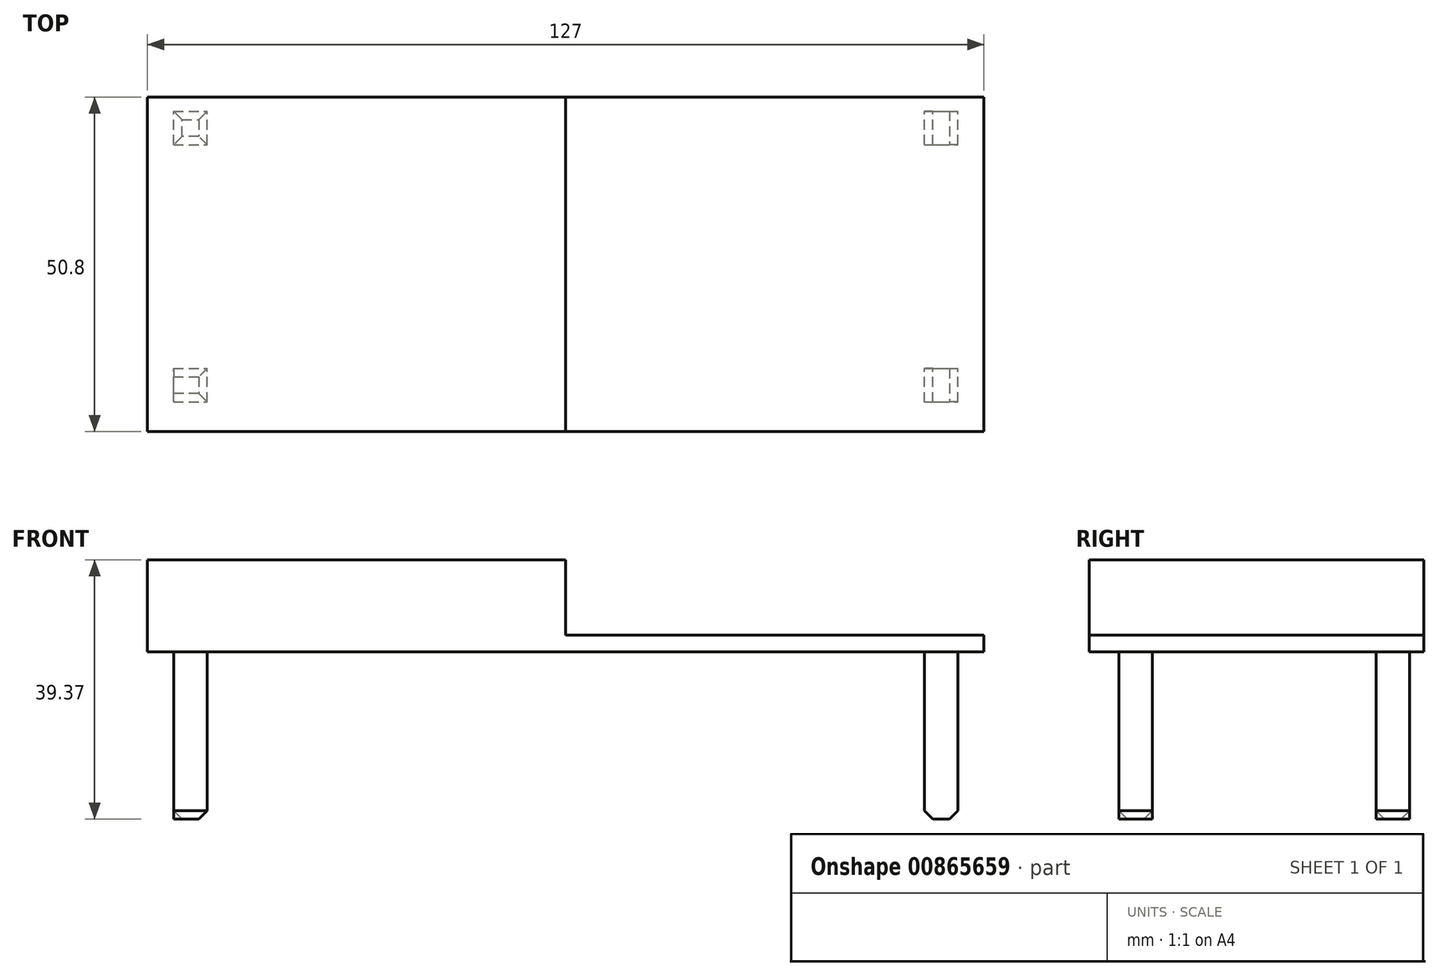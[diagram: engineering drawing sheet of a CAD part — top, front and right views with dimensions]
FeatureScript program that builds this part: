
annotation { "Feature Type Name" : "Feature", "Feature Type Description" : "" }
export const myFeature = defineFeature(function(context is Context, id is Id, definition is map)
    precondition{}
    {
        {
            var Q0;
            Q0=qCreatedBy(makeId("Top.planeOp"),FACE);
            var sketch = newSketch(context, id + "F0", { "sketchPlane" : qUnion([Q0])});
            skLineSegment(sketch, "E0.bottom", {"start": v(-63.73, 34.93) * mm, "end": v(63.27, 34.93) * mm});
            skLineSegment(sketch, "E0.top", {"start": v(-63.73, -15.87) * mm, "end": v(63.27, -15.87) * mm});
            skLineSegment(sketch, "E0.left", {"start": v(-63.73, 34.93) * mm, "end": v(-63.73, -15.87) * mm});
            skLineSegment(sketch, "E0.right", {"start": v(63.27, 34.93) * mm, "end": v(63.27, -15.87) * mm});
            skSolve(sketch);
        }
        {
            var Q0;
            Q0=makeQuery(id+"F0.imprint","IMPRINT",FACE,{"disambiguationData":[TD([[makeQuery(id+"F0.imprint","IMPRINT",EDGE,{"derivedFrom":sQuery(id+"F0.wireOp",EDGE,"E0.bottom")}),-1.0]])]});
            extrude(context, id + "F1", {"entities" : qUnion([Q0]), "depth" : 25.4 * mm, "offsetDistance" : 25.4 * mm});
        }
        {
            var Q0;
            Q0=makeQuery(id+"F1.opExtrude","CAP_FACE",FACE,{"disambiguationData":[OSD([sQuery(id+"F0.wireOp",EDGE,"E0.bottom"),sQuery(id+"F0.wireOp",EDGE,"E0.top"),sQuery(id+"F0.wireOp",EDGE,"E0.left"),sQuery(id+"F0.wireOp",EDGE,"E0.right")])],"isStart":false});
            var sketch = newSketch(context, id + "F2", { "sketchPlane" : qUnion([Q0])});
            skLineSegment(sketch, "E1.bottom", {"start": v(-0.23, 34.93) * mm, "end": v(63.27, 34.93) * mm});
            skLineSegment(sketch, "E1.top", {"start": v(-0.23, -15.87) * mm, "end": v(63.27, -15.87) * mm});
            skLineSegment(sketch, "E1.left", {"start": v(-0.23, 34.93) * mm, "end": v(-0.23, -15.87) * mm});
            skLineSegment(sketch, "E1.right", {"start": v(63.27, 34.93) * mm, "end": v(63.27, -15.87) * mm});
            skSolve(sketch);
        }
        {
            var Q0;
            Q0 = qSketchRegion(id + "F2", true);
            extrude(context, id + "F3", {"entities" : qUnion([Q0]), "operationType" : NewBodyOperationType.REMOVE, "oppositeDirection" : true, "depth" : 22.86 * mm, "offsetDistance" : 25.4 * mm});
        }
        {
            var Q0;
            Q0=makeQuery(id+"F1.opExtrude","CAP_FACE",FACE,{"disambiguationData":[OSD([sQuery(id+"F0.wireOp",EDGE,"E0.bottom"),sQuery(id+"F0.wireOp",EDGE,"E0.top"),sQuery(id+"F0.wireOp",EDGE,"E0.left"),sQuery(id+"F0.wireOp",EDGE,"E0.right")])],"isStart":true});
            var sketch = newSketch(context, id + "F4", { "sketchPlane" : qUnion([Q0])});
            skLineSegment(sketch, "E2.bottom", {"start": v(-59.76, 11.38) * mm, "end": v(-54.68, 11.38) * mm});
            skLineSegment(sketch, "E2.top", {"start": v(-59.76, 6.3) * mm, "end": v(-54.68, 6.3) * mm});
            skLineSegment(sketch, "E2.left", {"start": v(-59.76, 11.38) * mm, "end": v(-59.76, 6.3) * mm});
            skLineSegment(sketch, "E2.right", {"start": v(-54.68, 11.38) * mm, "end": v(-54.68, 6.3) * mm});
            skLineSegment(sketch, "E3", {"start": v(-54.68, -27.7) * mm, "end": v(-54.68, -32.78) * mm});
            skLineSegment(sketch, "E4", {"start": v(54.23, 6.3) * mm, "end": v(59.3, 6.3) * mm});
            skLineSegment(sketch, "E5.bottom", {"start": v(54.23, 11.38) * mm, "end": v(59.3, 11.38) * mm});
            skLineSegment(sketch, "E5.left", {"start": v(54.23, 11.38) * mm, "end": v(54.23, 6.3) * mm});
            skLineSegment(sketch, "E5.right", {"start": v(59.3, 11.38) * mm, "end": v(59.3, 6.3) * mm});
            skLineSegment(sketch, "E6", {"start": v(54.23, -27.7) * mm, "end": v(54.23, -32.78) * mm});
            skLineSegment(sketch, "E7", {"start": v(59.3, -27.7) * mm, "end": v(59.3, -32.78) * mm});
            skLineSegment(sketch, "E8.bottom", {"start": v(-59.76, -27.7) * mm, "end": v(-54.68, -27.7) * mm});
            skLineSegment(sketch, "E8.top", {"start": v(-59.76, -32.78) * mm, "end": v(-54.68, -32.78) * mm});
            skLineSegment(sketch, "E8.left", {"start": v(-59.76, -27.7) * mm, "end": v(-59.76, -32.78) * mm});
            skLineSegment(sketch, "E9", {"start": v(54.23, -27.7) * mm, "end": v(59.3, -27.7) * mm});
            skLineSegment(sketch, "E10", {"start": v(54.23, -32.78) * mm, "end": v(59.3, -32.78) * mm});
            skSolve(sketch);
        }
        {
            var Q0;
            Q0 = qSketchRegion(id + "F4", true);
            extrude(context, id + "F5", {"entities" : qUnion([Q0]), "operationType" : NewBodyOperationType.ADD, "depth" : 25.4 * mm, "offsetDistance" : 25.4 * mm});
        }
        {
            var Q0;
            Q0=makeQuery(id+"F5.opExtrude","CAP_EDGE",EDGE,{"disambiguationData":[OSD([sQuery(id+"F4.wireOp",EDGE,"E3")])],"isStart":false});
            var Q1;
            Q1=makeQuery(id+"F5.opExtrude","CAP_EDGE",EDGE,{"disambiguationData":[OSD([sQuery(id+"F4.wireOp",EDGE,"E8.bottom")])],"isStart":false});
            var Q2;
            Q2=makeQuery(id+"F5.opExtrude","CAP_EDGE",EDGE,{"disambiguationData":[OSD([sQuery(id+"F4.wireOp",EDGE,"E8.left")])],"isStart":false});
            var Q3;
            Q3=makeQuery(id+"F5.opExtrude","CAP_EDGE",EDGE,{"disambiguationData":[OSD([sQuery(id+"F4.wireOp",EDGE,"E8.top")])],"isStart":false});
            var Q4;
            Q4=makeQuery(id+"F5.opExtrude","CAP_EDGE",EDGE,{"disambiguationData":[OSD([sQuery(id+"F4.wireOp",EDGE,"E7")])],"isStart":false});
            var Q5;
            Q5=makeQuery(id+"F5.opExtrude","CAP_EDGE",EDGE,{"disambiguationData":[OSD([sQuery(id+"F4.wireOp",EDGE,"E10")])],"isStart":false});
            var Q6;
            Q6=makeQuery(id+"F5.opExtrude","CAP_EDGE",EDGE,{"disambiguationData":[OSD([sQuery(id+"F4.wireOp",EDGE,"E6")])],"isStart":false});
            var Q7;
            Q7=makeQuery(id+"F5.opExtrude","CAP_EDGE",EDGE,{"disambiguationData":[OSD([sQuery(id+"F4.wireOp",EDGE,"E9")])],"isStart":false});
            var Q8;
            Q8=makeQuery(id+"F5.opExtrude","CAP_EDGE",EDGE,{"disambiguationData":[OSD([sQuery(id+"F4.wireOp",EDGE,"E5.right")])],"isStart":false});
            var Q9;
            Q9=makeQuery(id+"F5.opExtrude","CAP_EDGE",EDGE,{"disambiguationData":[OSD([sQuery(id+"F4.wireOp",EDGE,"E4")])],"isStart":false});
            var Q10;
            Q10=makeQuery(id+"F5.opExtrude","CAP_EDGE",EDGE,{"disambiguationData":[OSD([sQuery(id+"F4.wireOp",EDGE,"E5.left")])],"isStart":false});
            var Q11;
            Q11=makeQuery(id+"F5.opExtrude","CAP_EDGE",EDGE,{"disambiguationData":[OSD([sQuery(id+"F4.wireOp",EDGE,"E5.bottom")])],"isStart":false});
            var Q12;
            Q12=makeQuery(id+"F5.opExtrude","CAP_EDGE",EDGE,{"disambiguationData":[OSD([sQuery(id+"F4.wireOp",EDGE,"E2.right")])],"isStart":false});
            var Q13;
            Q13=makeQuery(id+"F5.opExtrude","CAP_EDGE",EDGE,{"disambiguationData":[OSD([sQuery(id+"F4.wireOp",EDGE,"E2.top")])],"isStart":false});
            var Q14;
            Q14=makeQuery(id+"F5.opExtrude","CAP_EDGE",EDGE,{"disambiguationData":[OSD([sQuery(id+"F4.wireOp",EDGE,"E2.left")])],"isStart":false});
            var Q15;
            Q15=makeQuery(id+"F5.opExtrude","CAP_EDGE",EDGE,{"disambiguationData":[OSD([sQuery(id+"F4.wireOp",EDGE,"E2.bottom")])],"isStart":false});
            chamfer(context, id + "F6", {"entities" : qUnion([Q0, Q1, Q2, Q3, Q4, Q5, Q6, Q7, Q8, Q9, Q10, Q11, Q12, Q13, Q14, Q15]), "width" : 1.27 * mm, "tangentPropagation" : true});
        }
        {
            var Q0;
            Q0=makeQuery(id+"F1.opExtrude","SWEPT_FACE",FACE,{"disambiguationData":[OSD([sQuery(id+"F0.wireOp",EDGE,"E0.top")])]});
            var sketch = newSketch(context, id + "F7", { "sketchPlane" : qUnion([Q0])});
            skLineSegment(sketch, "E11.bottom", {"start": v(-63.73, 25.4) * mm, "end": v(-0.23, 25.4) * mm});
            skLineSegment(sketch, "E11.top", {"start": v(-63.73, 13.97) * mm, "end": v(-0.23, 13.97) * mm});
            skLineSegment(sketch, "E11.left", {"start": v(-63.73, 25.4) * mm, "end": v(-63.73, 13.97) * mm});
            skLineSegment(sketch, "E11.right", {"start": v(-0.23, 25.4) * mm, "end": v(-0.23, 13.97) * mm});
            skSolve(sketch);
        }
        {
            var Q0;
            Q0 = qSketchRegion(id + "F7", true);
            extrude(context, id + "F8", {"entities" : qUnion([Q0]), "operationType" : NewBodyOperationType.REMOVE, "oppositeDirection" : true, "depth" : 62.48 * mm, "offsetDistance" : 25.4 * mm});
        }
    });
